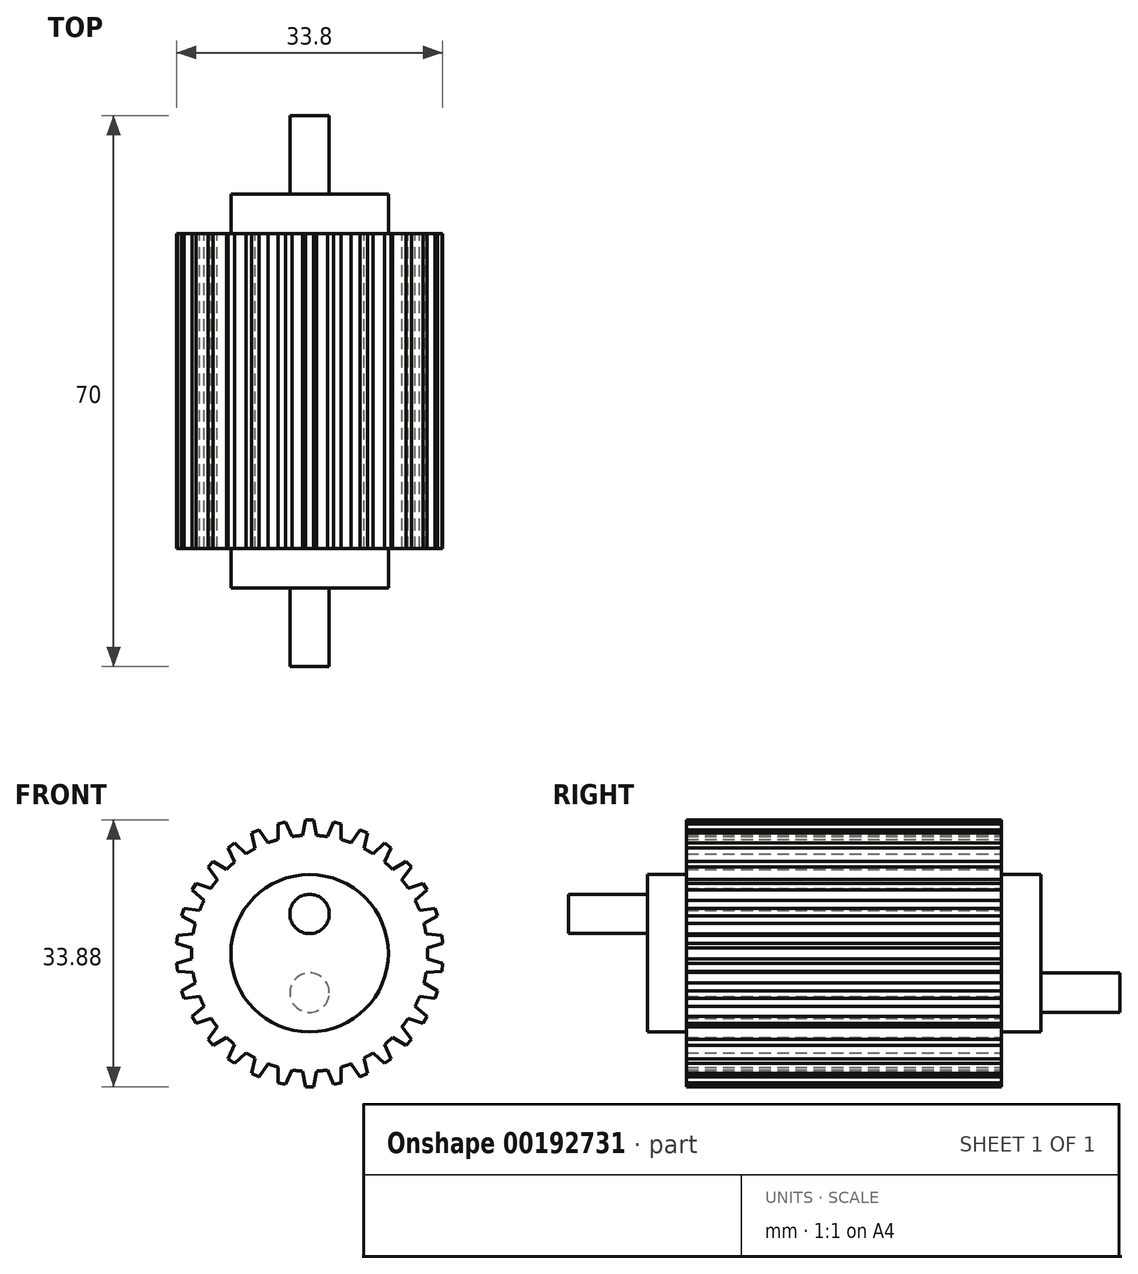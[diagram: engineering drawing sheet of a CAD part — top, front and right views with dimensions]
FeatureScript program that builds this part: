
annotation { "Feature Type Name" : "Feature", "Feature Type Description" : "" }
export const myFeature = defineFeature(function(context is Context, id is Id, definition is map)
    precondition{}
    {
        {
            var Q0;
            Q0=qCreatedBy(makeId("Front.planeOp"),FACE);
            var sketch = newSketch(context, id + "F0", { "sketchPlane" : qUnion([Q0])});
            skCircle(sketch, "E0", {"center": v(0, 0) * mm, "radius": 15 * mm});
            skLineSegment(sketch, "E1", {"start": v(0, 0) * mm, "end": v(0, 16.94) * mm, "construction": true});
            skLineSegment(sketch, "E2", {"start": v(0, 16.94) * mm, "end": v(-0.5, 16.94) * mm});
            skLineSegment(sketch, "E3", {"start": v(-0.5, 16.94) * mm, "end": v(-0.88, 14.97) * mm});
            skLineSegment(sketch, "E4.MirrorCS", {"start": v(0, 16.94) * mm, "end": v(0.5, 16.94) * mm});
            skLineSegment(sketch, "E5.MirrorCS", {"start": v(0.5, 16.94) * mm, "end": v(0.88, 14.97) * mm});
            skLineSegment(sketch, "E6.1.0", {"start": v(-4.01, 16.46) * mm, "end": v(-3.98, 14.46) * mm});
            skLineSegment(sketch, "E6.1.1", {"start": v(-3.52, 16.57) * mm, "end": v(-4.01, 16.46) * mm});
            skLineSegment(sketch, "E6.1.2", {"start": v(-3.52, 16.57) * mm, "end": v(-3.03, 16.67) * mm});
            skLineSegment(sketch, "E6.1.3", {"start": v(-3.03, 16.67) * mm, "end": v(-2.25, 14.83) * mm});
            skLineSegment(sketch, "E6.2.0", {"start": v(-7.35, 15.27) * mm, "end": v(-6.9, 13.32) * mm});
            skLineSegment(sketch, "E6.2.1", {"start": v(-6.89, 15.47) * mm, "end": v(-7.35, 15.27) * mm});
            skLineSegment(sketch, "E6.2.2", {"start": v(-6.89, 15.47) * mm, "end": v(-6.43, 15.68) * mm});
            skLineSegment(sketch, "E6.2.3", {"start": v(-6.43, 15.68) * mm, "end": v(-5.28, 14.04) * mm});
            skLineSegment(sketch, "E7.2.3.0", {"start": v(-10.36, 13.4) * mm, "end": v(-9.52, 11.6) * mm});
            skLineSegment(sketch, "E7.3.3.0", {"start": v(-9.96, 13.7) * mm, "end": v(-10.36, 13.4) * mm});
            skLineSegment(sketch, "E7.6.3.0", {"start": v(-9.96, 13.7) * mm, "end": v(-9.55, 14) * mm});
            skLineSegment(sketch, "E7.9.3.0", {"start": v(-9.55, 14) * mm, "end": v(-8.09, 12.63) * mm});
            skLineSegment(sketch, "E7.2.4.0", {"start": v(-12.92, 10.96) * mm, "end": v(-11.72, 9.36) * mm});
            skLineSegment(sketch, "E7.3.4.0", {"start": v(-12.59, 11.33) * mm, "end": v(-12.92, 10.96) * mm});
            skLineSegment(sketch, "E7.6.4.0", {"start": v(-12.59, 11.33) * mm, "end": v(-12.25, 11.7) * mm});
            skLineSegment(sketch, "E7.9.4.0", {"start": v(-12.25, 11.7) * mm, "end": v(-10.54, 10.68) * mm});
            skLineSegment(sketch, "E7.2.5.0", {"start": v(-14.92, 8.04) * mm, "end": v(-13.4, 6.72) * mm});
            skLineSegment(sketch, "E7.3.5.0", {"start": v(-14.67, 8.47) * mm, "end": v(-14.92, 8.04) * mm});
            skLineSegment(sketch, "E7.6.5.0", {"start": v(-14.67, 8.47) * mm, "end": v(-14.42, 8.9) * mm});
            skLineSegment(sketch, "E7.9.5.0", {"start": v(-14.42, 8.9) * mm, "end": v(-12.53, 8.25) * mm});
            skLineSegment(sketch, "E7.2.6.0", {"start": v(-16.26, 4.76) * mm, "end": v(-14.51, 3.79) * mm});
            skLineSegment(sketch, "E7.3.6.0", {"start": v(-16.1, 5.23) * mm, "end": v(-16.26, 4.76) * mm});
            skLineSegment(sketch, "E7.6.6.0", {"start": v(-16.1, 5.23) * mm, "end": v(-15.95, 5.7) * mm});
            skLineSegment(sketch, "E7.9.6.0", {"start": v(-15.95, 5.7) * mm, "end": v(-13.97, 5.47) * mm});
            skLineSegment(sketch, "E7.2.7.0", {"start": v(-16.9, 1.27) * mm, "end": v(-14.98, 0.69) * mm});
            skLineSegment(sketch, "E7.3.7.0", {"start": v(-16.84, 1.77) * mm, "end": v(-16.9, 1.27) * mm});
            skLineSegment(sketch, "E7.6.7.0", {"start": v(-16.84, 1.77) * mm, "end": v(-16.8, 2.27) * mm});
            skLineSegment(sketch, "E7.9.7.0", {"start": v(-16.8, 2.27) * mm, "end": v(-14.8, 2.44) * mm});
            skLineSegment(sketch, "E7.2.8.0", {"start": v(-16.8, -2.27) * mm, "end": v(-14.8, -2.44) * mm});
            skLineSegment(sketch, "E7.3.8.0", {"start": v(-16.84, -1.77) * mm, "end": v(-16.8, -2.27) * mm});
            skLineSegment(sketch, "E7.6.8.0", {"start": v(-16.84, -1.77) * mm, "end": v(-16.9, -1.27) * mm});
            skLineSegment(sketch, "E7.9.8.0", {"start": v(-16.9, -1.27) * mm, "end": v(-14.98, -0.69) * mm});
            skLineSegment(sketch, "E7.2.9.0", {"start": v(-15.95, -5.7) * mm, "end": v(-13.97, -5.47) * mm});
            skLineSegment(sketch, "E7.3.9.0", {"start": v(-16.1, -5.23) * mm, "end": v(-15.95, -5.7) * mm});
            skLineSegment(sketch, "E7.6.9.0", {"start": v(-16.1, -5.23) * mm, "end": v(-16.26, -4.76) * mm});
            skLineSegment(sketch, "E7.9.9.0", {"start": v(-16.26, -4.76) * mm, "end": v(-14.51, -3.79) * mm});
            skLineSegment(sketch, "E7.2.10.0", {"start": v(-14.42, -8.9) * mm, "end": v(-12.53, -8.25) * mm});
            skLineSegment(sketch, "E7.3.10.0", {"start": v(-14.67, -8.47) * mm, "end": v(-14.42, -8.9) * mm});
            skLineSegment(sketch, "E7.6.10.0", {"start": v(-14.67, -8.47) * mm, "end": v(-14.92, -8.04) * mm});
            skLineSegment(sketch, "E7.9.10.0", {"start": v(-14.92, -8.04) * mm, "end": v(-13.4, -6.72) * mm});
            skLineSegment(sketch, "E7.2.11.0", {"start": v(-12.25, -11.7) * mm, "end": v(-10.54, -10.68) * mm});
            skLineSegment(sketch, "E7.3.11.0", {"start": v(-12.59, -11.33) * mm, "end": v(-12.25, -11.7) * mm});
            skLineSegment(sketch, "E7.6.11.0", {"start": v(-12.59, -11.33) * mm, "end": v(-12.92, -10.96) * mm});
            skLineSegment(sketch, "E7.9.11.0", {"start": v(-12.92, -10.96) * mm, "end": v(-11.72, -9.36) * mm});
            skLineSegment(sketch, "E7.2.12.0", {"start": v(-9.55, -14) * mm, "end": v(-8.09, -12.63) * mm});
            skLineSegment(sketch, "E7.3.12.0", {"start": v(-9.96, -13.7) * mm, "end": v(-9.55, -14) * mm});
            skLineSegment(sketch, "E7.6.12.0", {"start": v(-9.96, -13.7) * mm, "end": v(-10.36, -13.4) * mm});
            skLineSegment(sketch, "E7.9.12.0", {"start": v(-10.36, -13.4) * mm, "end": v(-9.52, -11.6) * mm});
            skLineSegment(sketch, "E7.2.13.0", {"start": v(-6.43, -15.68) * mm, "end": v(-5.28, -14.04) * mm});
            skLineSegment(sketch, "E7.3.13.0", {"start": v(-6.89, -15.47) * mm, "end": v(-6.43, -15.68) * mm});
            skLineSegment(sketch, "E7.6.13.0", {"start": v(-6.89, -15.47) * mm, "end": v(-7.35, -15.27) * mm});
            skLineSegment(sketch, "E7.9.13.0", {"start": v(-7.35, -15.27) * mm, "end": v(-6.9, -13.32) * mm});
            skLineSegment(sketch, "E7.2.14.0", {"start": v(-3.03, -16.67) * mm, "end": v(-2.25, -14.83) * mm});
            skLineSegment(sketch, "E7.3.14.0", {"start": v(-3.52, -16.57) * mm, "end": v(-3.03, -16.67) * mm});
            skLineSegment(sketch, "E7.6.14.0", {"start": v(-3.52, -16.57) * mm, "end": v(-4.01, -16.46) * mm});
            skLineSegment(sketch, "E7.9.14.0", {"start": v(-4.01, -16.46) * mm, "end": v(-3.98, -14.46) * mm});
            skLineSegment(sketch, "E8.2.15.0", {"start": v(0.5, -16.94) * mm, "end": v(0.88, -14.97) * mm});
            skLineSegment(sketch, "E8.3.15.0", {"start": v(0, -16.94) * mm, "end": v(0.5, -16.94) * mm});
            skLineSegment(sketch, "E8.6.15.0", {"start": v(0, -16.94) * mm, "end": v(-0.5, -16.94) * mm});
            skLineSegment(sketch, "E8.9.15.0", {"start": v(-0.5, -16.94) * mm, "end": v(-0.88, -14.97) * mm});
            skLineSegment(sketch, "E8.2.16.0", {"start": v(4.01, -16.46) * mm, "end": v(3.98, -14.46) * mm});
            skLineSegment(sketch, "E8.3.16.0", {"start": v(3.52, -16.57) * mm, "end": v(4.01, -16.46) * mm});
            skLineSegment(sketch, "E8.6.16.0", {"start": v(3.52, -16.57) * mm, "end": v(3.03, -16.67) * mm});
            skLineSegment(sketch, "E8.9.16.0", {"start": v(3.03, -16.67) * mm, "end": v(2.25, -14.83) * mm});
            skLineSegment(sketch, "E8.2.17.0", {"start": v(7.35, -15.27) * mm, "end": v(6.9, -13.32) * mm});
            skLineSegment(sketch, "E8.3.17.0", {"start": v(6.89, -15.47) * mm, "end": v(7.35, -15.27) * mm});
            skLineSegment(sketch, "E8.6.17.0", {"start": v(6.89, -15.47) * mm, "end": v(6.43, -15.68) * mm});
            skLineSegment(sketch, "E8.9.17.0", {"start": v(6.43, -15.68) * mm, "end": v(5.28, -14.04) * mm});
            skLineSegment(sketch, "E8.2.18.0", {"start": v(10.36, -13.4) * mm, "end": v(9.52, -11.6) * mm});
            skLineSegment(sketch, "E8.3.18.0", {"start": v(9.96, -13.7) * mm, "end": v(10.36, -13.4) * mm});
            skLineSegment(sketch, "E8.6.18.0", {"start": v(9.96, -13.7) * mm, "end": v(9.55, -14) * mm});
            skLineSegment(sketch, "E8.9.18.0", {"start": v(9.55, -14) * mm, "end": v(8.09, -12.63) * mm});
            skLineSegment(sketch, "E8.2.19.0", {"start": v(12.92, -10.96) * mm, "end": v(11.72, -9.36) * mm});
            skLineSegment(sketch, "E8.3.19.0", {"start": v(12.59, -11.33) * mm, "end": v(12.92, -10.96) * mm});
            skLineSegment(sketch, "E8.6.19.0", {"start": v(12.59, -11.33) * mm, "end": v(12.25, -11.7) * mm});
            skLineSegment(sketch, "E8.9.19.0", {"start": v(12.25, -11.7) * mm, "end": v(10.54, -10.68) * mm});
            skLineSegment(sketch, "E8.2.20.0", {"start": v(14.92, -8.04) * mm, "end": v(13.4, -6.72) * mm});
            skLineSegment(sketch, "E8.3.20.0", {"start": v(14.67, -8.47) * mm, "end": v(14.92, -8.04) * mm});
            skLineSegment(sketch, "E8.6.20.0", {"start": v(14.67, -8.47) * mm, "end": v(14.42, -8.9) * mm});
            skLineSegment(sketch, "E8.9.20.0", {"start": v(14.42, -8.9) * mm, "end": v(12.53, -8.25) * mm});
            skLineSegment(sketch, "E8.2.21.0", {"start": v(16.26, -4.76) * mm, "end": v(14.51, -3.79) * mm});
            skLineSegment(sketch, "E8.3.21.0", {"start": v(16.1, -5.23) * mm, "end": v(16.26, -4.76) * mm});
            skLineSegment(sketch, "E8.6.21.0", {"start": v(16.1, -5.23) * mm, "end": v(15.95, -5.7) * mm});
            skLineSegment(sketch, "E8.9.21.0", {"start": v(15.95, -5.7) * mm, "end": v(13.97, -5.47) * mm});
            skLineSegment(sketch, "E8.2.22.0", {"start": v(16.9, -1.27) * mm, "end": v(14.98, -0.69) * mm});
            skLineSegment(sketch, "E8.3.22.0", {"start": v(16.84, -1.77) * mm, "end": v(16.9, -1.27) * mm});
            skLineSegment(sketch, "E8.6.22.0", {"start": v(16.84, -1.77) * mm, "end": v(16.8, -2.27) * mm});
            skLineSegment(sketch, "E8.9.22.0", {"start": v(16.8, -2.27) * mm, "end": v(14.8, -2.44) * mm});
            skLineSegment(sketch, "E8.2.23.0", {"start": v(16.8, 2.27) * mm, "end": v(14.8, 2.44) * mm});
            skLineSegment(sketch, "E8.3.23.0", {"start": v(16.84, 1.77) * mm, "end": v(16.8, 2.27) * mm});
            skLineSegment(sketch, "E8.6.23.0", {"start": v(16.84, 1.77) * mm, "end": v(16.9, 1.27) * mm});
            skLineSegment(sketch, "E8.9.23.0", {"start": v(16.9, 1.27) * mm, "end": v(14.98, 0.69) * mm});
            skLineSegment(sketch, "E8.2.24.0", {"start": v(15.95, 5.7) * mm, "end": v(13.97, 5.47) * mm});
            skLineSegment(sketch, "E8.3.24.0", {"start": v(16.1, 5.23) * mm, "end": v(15.95, 5.7) * mm});
            skLineSegment(sketch, "E8.6.24.0", {"start": v(16.1, 5.23) * mm, "end": v(16.26, 4.76) * mm});
            skLineSegment(sketch, "E8.9.24.0", {"start": v(16.26, 4.76) * mm, "end": v(14.51, 3.79) * mm});
            skLineSegment(sketch, "E9.2.25.0", {"start": v(14.42, 8.9) * mm, "end": v(12.53, 8.25) * mm});
            skLineSegment(sketch, "E9.3.25.0", {"start": v(14.67, 8.47) * mm, "end": v(14.42, 8.9) * mm});
            skLineSegment(sketch, "E9.6.25.0", {"start": v(14.67, 8.47) * mm, "end": v(14.92, 8.04) * mm});
            skLineSegment(sketch, "E9.9.25.0", {"start": v(14.92, 8.04) * mm, "end": v(13.4, 6.72) * mm});
            skLineSegment(sketch, "E9.2.26.0", {"start": v(12.25, 11.7) * mm, "end": v(10.54, 10.68) * mm});
            skLineSegment(sketch, "E9.3.26.0", {"start": v(12.59, 11.33) * mm, "end": v(12.25, 11.7) * mm});
            skLineSegment(sketch, "E9.6.26.0", {"start": v(12.59, 11.33) * mm, "end": v(12.92, 10.96) * mm});
            skLineSegment(sketch, "E9.9.26.0", {"start": v(12.92, 10.96) * mm, "end": v(11.72, 9.36) * mm});
            skLineSegment(sketch, "E9.2.27.0", {"start": v(9.55, 14) * mm, "end": v(8.09, 12.63) * mm});
            skLineSegment(sketch, "E9.3.27.0", {"start": v(9.96, 13.7) * mm, "end": v(9.55, 14) * mm});
            skLineSegment(sketch, "E9.6.27.0", {"start": v(9.96, 13.7) * mm, "end": v(10.36, 13.4) * mm});
            skLineSegment(sketch, "E9.9.27.0", {"start": v(10.36, 13.4) * mm, "end": v(9.52, 11.6) * mm});
            skLineSegment(sketch, "E9.2.28.0", {"start": v(6.43, 15.68) * mm, "end": v(5.28, 14.04) * mm});
            skLineSegment(sketch, "E9.3.28.0", {"start": v(6.89, 15.47) * mm, "end": v(6.43, 15.68) * mm});
            skLineSegment(sketch, "E9.6.28.0", {"start": v(6.89, 15.47) * mm, "end": v(7.35, 15.27) * mm});
            skLineSegment(sketch, "E9.9.28.0", {"start": v(7.35, 15.27) * mm, "end": v(6.9, 13.32) * mm});
            skLineSegment(sketch, "E9.2.29.0", {"start": v(3.03, 16.67) * mm, "end": v(2.25, 14.83) * mm});
            skLineSegment(sketch, "E9.3.29.0", {"start": v(3.52, 16.57) * mm, "end": v(3.03, 16.67) * mm});
            skLineSegment(sketch, "E9.6.29.0", {"start": v(3.52, 16.57) * mm, "end": v(4.01, 16.46) * mm});
            skLineSegment(sketch, "E9.9.29.0", {"start": v(4.01, 16.46) * mm, "end": v(3.98, 14.46) * mm});
            skSolve(sketch);
        }
        {
            var Q0;
            Q0 = qSketchRegion(id + "F0", true);
            extrude(context, id + "F1", {"entities" : qUnion([Q0]), "depth" : 40 * mm});
        }
        {
            var Q0;
            Q0=makeQuery(id+"F1.opExtrude","CAP_FACE",FACE,{"disambiguationData":[OSD([sQuery(id+"F0.wireOp",EDGE,"E0"),sQuery(id+"F0.wireOp",EDGE,"E2"),sQuery(id+"F0.wireOp",EDGE,"E3"),sQuery(id+"F0.wireOp",EDGE,"E4.MirrorCS"),sQuery(id+"F0.wireOp",EDGE,"E5.MirrorCS"),sQuery(id+"F0.wireOp",EDGE,"E6.1.0"),sQuery(id+"F0.wireOp",EDGE,"E6.1.1"),sQuery(id+"F0.wireOp",EDGE,"E6.1.2"),sQuery(id+"F0.wireOp",EDGE,"E6.1.3"),sQuery(id+"F0.wireOp",EDGE,"E6.2.0"),sQuery(id+"F0.wireOp",EDGE,"E6.2.1"),sQuery(id+"F0.wireOp",EDGE,"E6.2.2"),sQuery(id+"F0.wireOp",EDGE,"E6.2.3"),sQuery(id+"F0.wireOp",EDGE,"E7.2.3.0"),sQuery(id+"F0.wireOp",EDGE,"E7.3.3.0"),sQuery(id+"F0.wireOp",EDGE,"E7.6.3.0"),sQuery(id+"F0.wireOp",EDGE,"E7.9.3.0"),sQuery(id+"F0.wireOp",EDGE,"E7.2.4.0"),sQuery(id+"F0.wireOp",EDGE,"E7.3.4.0"),sQuery(id+"F0.wireOp",EDGE,"E7.6.4.0"),sQuery(id+"F0.wireOp",EDGE,"E7.9.4.0"),sQuery(id+"F0.wireOp",EDGE,"E7.2.5.0"),sQuery(id+"F0.wireOp",EDGE,"E7.3.5.0"),sQuery(id+"F0.wireOp",EDGE,"E7.6.5.0"),sQuery(id+"F0.wireOp",EDGE,"E7.9.5.0"),sQuery(id+"F0.wireOp",EDGE,"E7.2.6.0"),sQuery(id+"F0.wireOp",EDGE,"E7.3.6.0"),sQuery(id+"F0.wireOp",EDGE,"E7.6.6.0"),sQuery(id+"F0.wireOp",EDGE,"E7.9.6.0"),sQuery(id+"F0.wireOp",EDGE,"E7.2.7.0"),sQuery(id+"F0.wireOp",EDGE,"E7.3.7.0"),sQuery(id+"F0.wireOp",EDGE,"E7.6.7.0"),sQuery(id+"F0.wireOp",EDGE,"E7.9.7.0"),sQuery(id+"F0.wireOp",EDGE,"E7.2.8.0"),sQuery(id+"F0.wireOp",EDGE,"E7.3.8.0"),sQuery(id+"F0.wireOp",EDGE,"E7.6.8.0"),sQuery(id+"F0.wireOp",EDGE,"E7.9.8.0"),sQuery(id+"F0.wireOp",EDGE,"E7.2.9.0"),sQuery(id+"F0.wireOp",EDGE,"E7.3.9.0"),sQuery(id+"F0.wireOp",EDGE,"E7.6.9.0"),sQuery(id+"F0.wireOp",EDGE,"E7.9.9.0"),sQuery(id+"F0.wireOp",EDGE,"E7.2.10.0"),sQuery(id+"F0.wireOp",EDGE,"E7.3.10.0"),sQuery(id+"F0.wireOp",EDGE,"E7.6.10.0"),sQuery(id+"F0.wireOp",EDGE,"E7.9.10.0"),sQuery(id+"F0.wireOp",EDGE,"E7.2.11.0"),sQuery(id+"F0.wireOp",EDGE,"E7.3.11.0"),sQuery(id+"F0.wireOp",EDGE,"E7.6.11.0"),sQuery(id+"F0.wireOp",EDGE,"E7.9.11.0"),sQuery(id+"F0.wireOp",EDGE,"E7.2.12.0"),sQuery(id+"F0.wireOp",EDGE,"E7.3.12.0"),sQuery(id+"F0.wireOp",EDGE,"E7.6.12.0"),sQuery(id+"F0.wireOp",EDGE,"E7.9.12.0"),sQuery(id+"F0.wireOp",EDGE,"E7.2.13.0"),sQuery(id+"F0.wireOp",EDGE,"E7.3.13.0"),sQuery(id+"F0.wireOp",EDGE,"E7.6.13.0"),sQuery(id+"F0.wireOp",EDGE,"E7.9.13.0"),sQuery(id+"F0.wireOp",EDGE,"E7.2.14.0"),sQuery(id+"F0.wireOp",EDGE,"E7.3.14.0"),sQuery(id+"F0.wireOp",EDGE,"E7.6.14.0"),sQuery(id+"F0.wireOp",EDGE,"E7.9.14.0"),sQuery(id+"F0.wireOp",EDGE,"E8.2.15.0"),sQuery(id+"F0.wireOp",EDGE,"E8.3.15.0"),sQuery(id+"F0.wireOp",EDGE,"E8.6.15.0"),sQuery(id+"F0.wireOp",EDGE,"E8.9.15.0"),sQuery(id+"F0.wireOp",EDGE,"E8.2.16.0"),sQuery(id+"F0.wireOp",EDGE,"E8.3.16.0"),sQuery(id+"F0.wireOp",EDGE,"E8.6.16.0"),sQuery(id+"F0.wireOp",EDGE,"E8.9.16.0"),sQuery(id+"F0.wireOp",EDGE,"E8.2.17.0"),sQuery(id+"F0.wireOp",EDGE,"E8.3.17.0"),sQuery(id+"F0.wireOp",EDGE,"E8.6.17.0"),sQuery(id+"F0.wireOp",EDGE,"E8.9.17.0"),sQuery(id+"F0.wireOp",EDGE,"E8.2.18.0"),sQuery(id+"F0.wireOp",EDGE,"E8.3.18.0"),sQuery(id+"F0.wireOp",EDGE,"E8.6.18.0"),sQuery(id+"F0.wireOp",EDGE,"E8.9.18.0"),sQuery(id+"F0.wireOp",EDGE,"E8.2.19.0"),sQuery(id+"F0.wireOp",EDGE,"E8.3.19.0"),sQuery(id+"F0.wireOp",EDGE,"E8.6.19.0"),sQuery(id+"F0.wireOp",EDGE,"E8.9.19.0"),sQuery(id+"F0.wireOp",EDGE,"E8.2.20.0"),sQuery(id+"F0.wireOp",EDGE,"E8.3.20.0"),sQuery(id+"F0.wireOp",EDGE,"E8.6.20.0"),sQuery(id+"F0.wireOp",EDGE,"E8.9.20.0"),sQuery(id+"F0.wireOp",EDGE,"E8.2.21.0"),sQuery(id+"F0.wireOp",EDGE,"E8.3.21.0"),sQuery(id+"F0.wireOp",EDGE,"E8.6.21.0"),sQuery(id+"F0.wireOp",EDGE,"E8.9.21.0"),sQuery(id+"F0.wireOp",EDGE,"E8.2.22.0"),sQuery(id+"F0.wireOp",EDGE,"E8.3.22.0"),sQuery(id+"F0.wireOp",EDGE,"E8.6.22.0"),sQuery(id+"F0.wireOp",EDGE,"E8.9.22.0"),sQuery(id+"F0.wireOp",EDGE,"E8.2.23.0"),sQuery(id+"F0.wireOp",EDGE,"E8.3.23.0"),sQuery(id+"F0.wireOp",EDGE,"E8.6.23.0"),sQuery(id+"F0.wireOp",EDGE,"E8.9.23.0"),sQuery(id+"F0.wireOp",EDGE,"E8.2.24.0"),sQuery(id+"F0.wireOp",EDGE,"E8.3.24.0"),sQuery(id+"F0.wireOp",EDGE,"E8.6.24.0"),sQuery(id+"F0.wireOp",EDGE,"E8.9.24.0"),sQuery(id+"F0.wireOp",EDGE,"E9.2.25.0"),sQuery(id+"F0.wireOp",EDGE,"E9.3.25.0"),sQuery(id+"F0.wireOp",EDGE,"E9.6.25.0"),sQuery(id+"F0.wireOp",EDGE,"E9.9.25.0"),sQuery(id+"F0.wireOp",EDGE,"E9.2.26.0"),sQuery(id+"F0.wireOp",EDGE,"E9.3.26.0"),sQuery(id+"F0.wireOp",EDGE,"E9.6.26.0"),sQuery(id+"F0.wireOp",EDGE,"E9.9.26.0"),sQuery(id+"F0.wireOp",EDGE,"E9.2.27.0"),sQuery(id+"F0.wireOp",EDGE,"E9.3.27.0"),sQuery(id+"F0.wireOp",EDGE,"E9.6.27.0"),sQuery(id+"F0.wireOp",EDGE,"E9.9.27.0"),sQuery(id+"F0.wireOp",EDGE,"E9.2.28.0"),sQuery(id+"F0.wireOp",EDGE,"E9.3.28.0"),sQuery(id+"F0.wireOp",EDGE,"E9.6.28.0"),sQuery(id+"F0.wireOp",EDGE,"E9.9.28.0"),sQuery(id+"F0.wireOp",EDGE,"E9.2.29.0"),sQuery(id+"F0.wireOp",EDGE,"E9.3.29.0"),sQuery(id+"F0.wireOp",EDGE,"E9.6.29.0"),sQuery(id+"F0.wireOp",EDGE,"E9.9.29.0")])],"isStart":true});
            var sketch = newSketch(context, id + "F2", { "sketchPlane" : qUnion([Q0])});
            skCircle(sketch, "E10", {"center": v(0, 0) * mm, "radius": 10 * mm});
            skSolve(sketch);
        }
        {
            var Q0;
            Q0 = qSketchRegion(id + "F2", true);
            extrude(context, id + "F3", {"entities" : qUnion([Q0]), "operationType" : NewBodyOperationType.ADD, "depth" : 5 * mm});
        }
        {
            var Q0;
            Q0=makeQuery(id+"F1.opExtrude","CAP_FACE",FACE,{"disambiguationData":[OSD([sQuery(id+"F0.wireOp",EDGE,"E0"),sQuery(id+"F0.wireOp",EDGE,"E2"),sQuery(id+"F0.wireOp",EDGE,"E3"),sQuery(id+"F0.wireOp",EDGE,"E4.MirrorCS"),sQuery(id+"F0.wireOp",EDGE,"E5.MirrorCS"),sQuery(id+"F0.wireOp",EDGE,"E6.1.0"),sQuery(id+"F0.wireOp",EDGE,"E6.1.1"),sQuery(id+"F0.wireOp",EDGE,"E6.1.2"),sQuery(id+"F0.wireOp",EDGE,"E6.1.3"),sQuery(id+"F0.wireOp",EDGE,"E6.2.0"),sQuery(id+"F0.wireOp",EDGE,"E6.2.1"),sQuery(id+"F0.wireOp",EDGE,"E6.2.2"),sQuery(id+"F0.wireOp",EDGE,"E6.2.3"),sQuery(id+"F0.wireOp",EDGE,"E7.2.3.0"),sQuery(id+"F0.wireOp",EDGE,"E7.3.3.0"),sQuery(id+"F0.wireOp",EDGE,"E7.6.3.0"),sQuery(id+"F0.wireOp",EDGE,"E7.9.3.0"),sQuery(id+"F0.wireOp",EDGE,"E7.2.4.0"),sQuery(id+"F0.wireOp",EDGE,"E7.3.4.0"),sQuery(id+"F0.wireOp",EDGE,"E7.6.4.0"),sQuery(id+"F0.wireOp",EDGE,"E7.9.4.0"),sQuery(id+"F0.wireOp",EDGE,"E7.2.5.0"),sQuery(id+"F0.wireOp",EDGE,"E7.3.5.0"),sQuery(id+"F0.wireOp",EDGE,"E7.6.5.0"),sQuery(id+"F0.wireOp",EDGE,"E7.9.5.0"),sQuery(id+"F0.wireOp",EDGE,"E7.2.6.0"),sQuery(id+"F0.wireOp",EDGE,"E7.3.6.0"),sQuery(id+"F0.wireOp",EDGE,"E7.6.6.0"),sQuery(id+"F0.wireOp",EDGE,"E7.9.6.0"),sQuery(id+"F0.wireOp",EDGE,"E7.2.7.0"),sQuery(id+"F0.wireOp",EDGE,"E7.3.7.0"),sQuery(id+"F0.wireOp",EDGE,"E7.6.7.0"),sQuery(id+"F0.wireOp",EDGE,"E7.9.7.0"),sQuery(id+"F0.wireOp",EDGE,"E7.2.8.0"),sQuery(id+"F0.wireOp",EDGE,"E7.3.8.0"),sQuery(id+"F0.wireOp",EDGE,"E7.6.8.0"),sQuery(id+"F0.wireOp",EDGE,"E7.9.8.0"),sQuery(id+"F0.wireOp",EDGE,"E7.2.9.0"),sQuery(id+"F0.wireOp",EDGE,"E7.3.9.0"),sQuery(id+"F0.wireOp",EDGE,"E7.6.9.0"),sQuery(id+"F0.wireOp",EDGE,"E7.9.9.0"),sQuery(id+"F0.wireOp",EDGE,"E7.2.10.0"),sQuery(id+"F0.wireOp",EDGE,"E7.3.10.0"),sQuery(id+"F0.wireOp",EDGE,"E7.6.10.0"),sQuery(id+"F0.wireOp",EDGE,"E7.9.10.0"),sQuery(id+"F0.wireOp",EDGE,"E7.2.11.0"),sQuery(id+"F0.wireOp",EDGE,"E7.3.11.0"),sQuery(id+"F0.wireOp",EDGE,"E7.6.11.0"),sQuery(id+"F0.wireOp",EDGE,"E7.9.11.0"),sQuery(id+"F0.wireOp",EDGE,"E7.2.12.0"),sQuery(id+"F0.wireOp",EDGE,"E7.3.12.0"),sQuery(id+"F0.wireOp",EDGE,"E7.6.12.0"),sQuery(id+"F0.wireOp",EDGE,"E7.9.12.0"),sQuery(id+"F0.wireOp",EDGE,"E7.2.13.0"),sQuery(id+"F0.wireOp",EDGE,"E7.3.13.0"),sQuery(id+"F0.wireOp",EDGE,"E7.6.13.0"),sQuery(id+"F0.wireOp",EDGE,"E7.9.13.0"),sQuery(id+"F0.wireOp",EDGE,"E7.2.14.0"),sQuery(id+"F0.wireOp",EDGE,"E7.3.14.0"),sQuery(id+"F0.wireOp",EDGE,"E7.6.14.0"),sQuery(id+"F0.wireOp",EDGE,"E7.9.14.0"),sQuery(id+"F0.wireOp",EDGE,"E8.2.15.0"),sQuery(id+"F0.wireOp",EDGE,"E8.3.15.0"),sQuery(id+"F0.wireOp",EDGE,"E8.6.15.0"),sQuery(id+"F0.wireOp",EDGE,"E8.9.15.0"),sQuery(id+"F0.wireOp",EDGE,"E8.2.16.0"),sQuery(id+"F0.wireOp",EDGE,"E8.3.16.0"),sQuery(id+"F0.wireOp",EDGE,"E8.6.16.0"),sQuery(id+"F0.wireOp",EDGE,"E8.9.16.0"),sQuery(id+"F0.wireOp",EDGE,"E8.2.17.0"),sQuery(id+"F0.wireOp",EDGE,"E8.3.17.0"),sQuery(id+"F0.wireOp",EDGE,"E8.6.17.0"),sQuery(id+"F0.wireOp",EDGE,"E8.9.17.0"),sQuery(id+"F0.wireOp",EDGE,"E8.2.18.0"),sQuery(id+"F0.wireOp",EDGE,"E8.3.18.0"),sQuery(id+"F0.wireOp",EDGE,"E8.6.18.0"),sQuery(id+"F0.wireOp",EDGE,"E8.9.18.0"),sQuery(id+"F0.wireOp",EDGE,"E8.2.19.0"),sQuery(id+"F0.wireOp",EDGE,"E8.3.19.0"),sQuery(id+"F0.wireOp",EDGE,"E8.6.19.0"),sQuery(id+"F0.wireOp",EDGE,"E8.9.19.0"),sQuery(id+"F0.wireOp",EDGE,"E8.2.20.0"),sQuery(id+"F0.wireOp",EDGE,"E8.3.20.0"),sQuery(id+"F0.wireOp",EDGE,"E8.6.20.0"),sQuery(id+"F0.wireOp",EDGE,"E8.9.20.0"),sQuery(id+"F0.wireOp",EDGE,"E8.2.21.0"),sQuery(id+"F0.wireOp",EDGE,"E8.3.21.0"),sQuery(id+"F0.wireOp",EDGE,"E8.6.21.0"),sQuery(id+"F0.wireOp",EDGE,"E8.9.21.0"),sQuery(id+"F0.wireOp",EDGE,"E8.2.22.0"),sQuery(id+"F0.wireOp",EDGE,"E8.3.22.0"),sQuery(id+"F0.wireOp",EDGE,"E8.6.22.0"),sQuery(id+"F0.wireOp",EDGE,"E8.9.22.0"),sQuery(id+"F0.wireOp",EDGE,"E8.2.23.0"),sQuery(id+"F0.wireOp",EDGE,"E8.3.23.0"),sQuery(id+"F0.wireOp",EDGE,"E8.6.23.0"),sQuery(id+"F0.wireOp",EDGE,"E8.9.23.0"),sQuery(id+"F0.wireOp",EDGE,"E8.2.24.0"),sQuery(id+"F0.wireOp",EDGE,"E8.3.24.0"),sQuery(id+"F0.wireOp",EDGE,"E8.6.24.0"),sQuery(id+"F0.wireOp",EDGE,"E8.9.24.0"),sQuery(id+"F0.wireOp",EDGE,"E9.2.25.0"),sQuery(id+"F0.wireOp",EDGE,"E9.3.25.0"),sQuery(id+"F0.wireOp",EDGE,"E9.6.25.0"),sQuery(id+"F0.wireOp",EDGE,"E9.9.25.0"),sQuery(id+"F0.wireOp",EDGE,"E9.2.26.0"),sQuery(id+"F0.wireOp",EDGE,"E9.3.26.0"),sQuery(id+"F0.wireOp",EDGE,"E9.6.26.0"),sQuery(id+"F0.wireOp",EDGE,"E9.9.26.0"),sQuery(id+"F0.wireOp",EDGE,"E9.2.27.0"),sQuery(id+"F0.wireOp",EDGE,"E9.3.27.0"),sQuery(id+"F0.wireOp",EDGE,"E9.6.27.0"),sQuery(id+"F0.wireOp",EDGE,"E9.9.27.0"),sQuery(id+"F0.wireOp",EDGE,"E9.2.28.0"),sQuery(id+"F0.wireOp",EDGE,"E9.3.28.0"),sQuery(id+"F0.wireOp",EDGE,"E9.6.28.0"),sQuery(id+"F0.wireOp",EDGE,"E9.9.28.0"),sQuery(id+"F0.wireOp",EDGE,"E9.2.29.0"),sQuery(id+"F0.wireOp",EDGE,"E9.3.29.0"),sQuery(id+"F0.wireOp",EDGE,"E9.6.29.0"),sQuery(id+"F0.wireOp",EDGE,"E9.9.29.0")])],"isStart":false});
            var sketch = newSketch(context, id + "F4", { "sketchPlane" : qUnion([Q0])});
            skCircle(sketch, "E11", {"center": v(0, 0) * mm, "radius": 10 * mm});
            skSolve(sketch);
        }
        {
            var Q0;
            Q0 = qSketchRegion(id + "F4", true);
            extrude(context, id + "F5", {"entities" : qUnion([Q0]), "operationType" : NewBodyOperationType.ADD, "depth" : 5 * mm});
        }
        {
            var Q0;
            Q0=makeQuery(id+"F5.opExtrude","CAP_FACE",FACE,{"disambiguationData":[OSD([sQuery(id+"F4.wireOp",EDGE,"E11")])],"isStart":false});
            var sketch = newSketch(context, id + "F6", { "sketchPlane" : qUnion([Q0])});
            skLineSegment(sketch, "E12", {"start": v(0, 0) * mm, "end": v(0, 10) * mm, "construction": true});
            skCircle(sketch, "E13", {"center": v(0, 5) * mm, "radius": 2.5 * mm});
            skSolve(sketch);
        }
        {
            var Q0;
            Q0 = qSketchRegion(id + "F6", true);
            extrude(context, id + "F7", {"entities" : qUnion([Q0]), "operationType" : NewBodyOperationType.ADD, "depth" : 10 * mm});
        }
        {
            var Q0;
            Q0=makeQuery(id+"F3.opExtrude","CAP_FACE",FACE,{"disambiguationData":[OSD([sQuery(id+"F2.wireOp",EDGE,"E10")])],"isStart":false});
            var sketch = newSketch(context, id + "F8", { "sketchPlane" : qUnion([Q0])});
            skLineSegment(sketch, "E14", {"start": v(0, 0) * mm, "end": v(0, -10) * mm, "construction": true});
            skCircle(sketch, "E15", {"center": v(0, -5) * mm, "radius": 2.5 * mm});
            skSolve(sketch);
        }
        {
            var Q0;
            Q0 = qSketchRegion(id + "F8", true);
            extrude(context, id + "F9", {"entities" : qUnion([Q0]), "operationType" : NewBodyOperationType.ADD, "depth" : 10 * mm});
        }
    });
